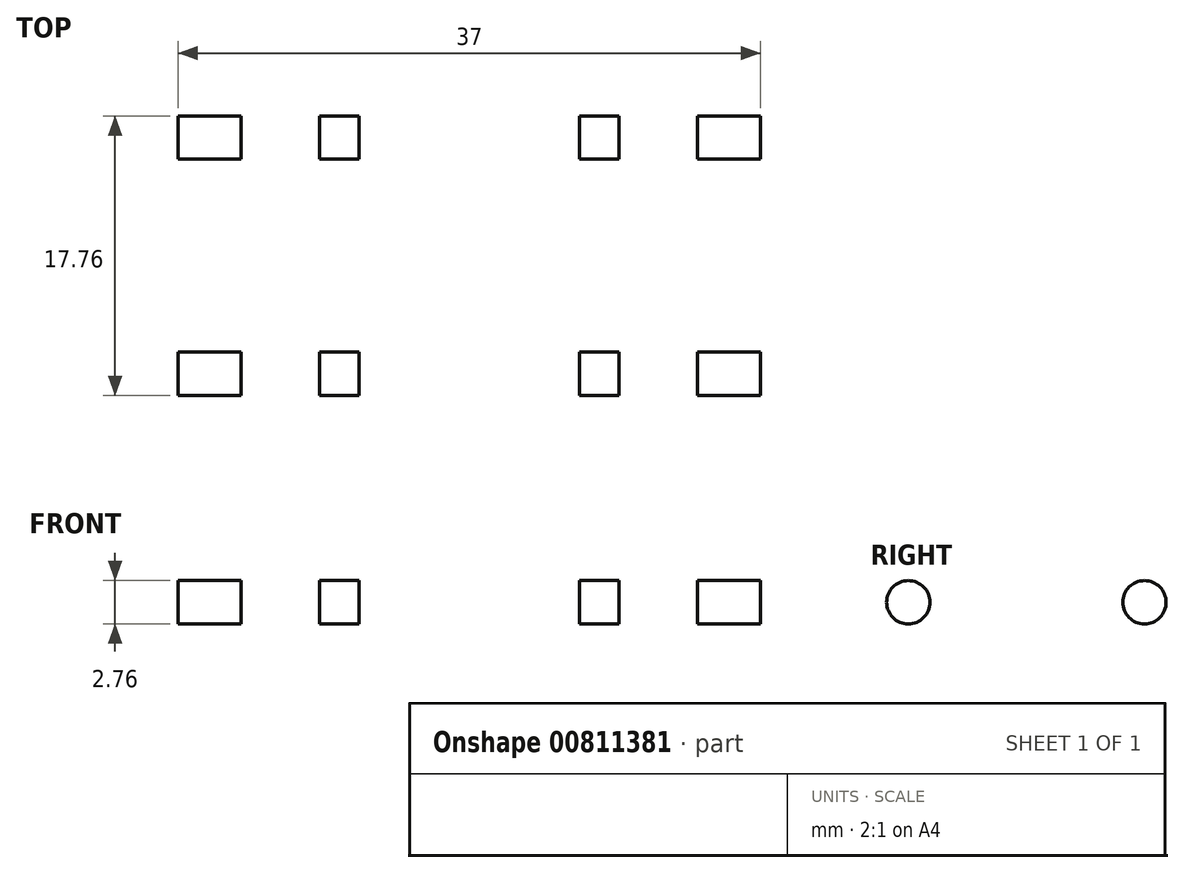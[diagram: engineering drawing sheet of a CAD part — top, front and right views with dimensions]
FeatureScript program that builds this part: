
annotation { "Feature Type Name" : "Feature", "Feature Type Description" : "" }
export const myFeature = defineFeature(function(context is Context, id is Id, definition is map)
    precondition{}
    {
        {
            var Q0;
            Q0=qCreatedBy(makeId("Front.planeOp"),FACE);
            var sketch = newSketch(context, id + "F0", { "sketchPlane" : qUnion([Q0])});
            skLineSegment(sketch, "E0.bottom", {"start": v(18.5, -7.5) * mm, "end": v(-18.5, -7.5) * mm});
            skLineSegment(sketch, "E0.top", {"start": v(18.5, 7.5) * mm, "end": v(-18.5, 7.5) * mm});
            skLineSegment(sketch, "E0.left", {"start": v(18.5, -7.5) * mm, "end": v(18.5, 7.5) * mm});
            skLineSegment(sketch, "E0.right", {"start": v(-18.5, -7.5) * mm, "end": v(-18.5, 7.5) * mm});
            skPoint(sketch, "E0.middle", {"position": v(0, 0) * mm});
            skLineSegment(sketch, "E1.bottom", {"start": v(-10, 7.5) * mm, "end": v(10, 7.5) * mm});
            skLineSegment(sketch, "E1.top", {"start": v(-10, 17.5) * mm, "end": v(10, 17.5) * mm});
            skLineSegment(sketch, "E1.left", {"start": v(-10, 7.5) * mm, "end": v(-10, 17.5) * mm});
            skLineSegment(sketch, "E1.right", {"start": v(10, 7.5) * mm, "end": v(10, 17.5) * mm});
            skLineSegment(sketch, "E2.bottom", {"start": v(-3.5, 17.5) * mm, "end": v(3.5, 17.5) * mm});
            skLineSegment(sketch, "E2.top", {"start": v(-3.5, 7.5) * mm, "end": v(3.5, 7.5) * mm});
            skLineSegment(sketch, "E2.left", {"start": v(-3.5, 17.5) * mm, "end": v(-3.5, 7.5) * mm});
            skLineSegment(sketch, "E2.right", {"start": v(3.5, 17.5) * mm, "end": v(3.5, 7.5) * mm});
            skLineSegment(sketch, "E3.bottom", {"start": v(-14.5, 2.5) * mm, "end": v(-9.5, 2.5) * mm});
            skLineSegment(sketch, "E3.top", {"start": v(-14.5, -2.5) * mm, "end": v(-9.5, -2.5) * mm});
            skLineSegment(sketch, "E3.left", {"start": v(-14.5, 2.5) * mm, "end": v(-14.5, -2.5) * mm});
            skLineSegment(sketch, "E3.right", {"start": v(-9.5, 2.5) * mm, "end": v(-9.5, -2.5) * mm});
            skLineSegment(sketch, "E4.bottom", {"start": v(9.5, 2.5) * mm, "end": v(14.5, 2.5) * mm});
            skLineSegment(sketch, "E4.top", {"start": v(9.5, -2.5) * mm, "end": v(14.5, -2.5) * mm});
            skLineSegment(sketch, "E4.left", {"start": v(9.5, 2.5) * mm, "end": v(9.5, -2.5) * mm});
            skLineSegment(sketch, "E4.right", {"start": v(14.5, 2.5) * mm, "end": v(14.5, -2.5) * mm});
            skLineSegment(sketch, "E5.bottom", {"start": v(7, -2.5) * mm, "end": v(-7, -2.5) * mm});
            skLineSegment(sketch, "E5.top", {"start": v(7, 2.5) * mm, "end": v(-7, 2.5) * mm});
            skLineSegment(sketch, "E5.left", {"start": v(7, -2.5) * mm, "end": v(7, 2.5) * mm});
            skLineSegment(sketch, "E5.right", {"start": v(-7, -2.5) * mm, "end": v(-7, 2.5) * mm});
            skSolve(sketch);
        }
        {
            var Q0;
            Q0=makeQuery(id+"F0.imprint","IMPRINT",FACE,{"disambiguationData":[TD([[makeQuery(id+"F0.imprint","IMPRINT",EDGE,{"derivedFrom":sQuery(id+"F0.wireOp",EDGE,"E0.bottom")}),-1.0]])]});
            var Q1;
            Q1=makeQuery(id+"F0.imprint","IMPRINT",FACE,{"disambiguationData":[TD([[makeQuery(id+"F0.imprint","IMPRINT",EDGE,{"derivedFrom":sQuery(id+"F0.wireOp",EDGE,"E1.bottom")}),1.0]])]});
            extrude(context, id + "F1", {"entities" : qUnion([Q0, Q1]), "depth" : 25 * mm, "offsetDistance" : 25 * mm});
        }
        {
            var Q0;
            Q0=makeQuery(id+"F1.opExtrude","SWEPT_FACE",FACE,{"disambiguationData":[OSD([sQuery(id+"F0.wireOp",EDGE,"E0.right")])]});
            var sketch = newSketch(context, id + "F2", { "sketchPlane" : qUnion([Q0])});
            skLineSegment(sketch, "E6", {"start": v(25, 0) * mm, "end": v(0, 0) * mm});
            skCircle(sketch, "E7", {"center": v(5, 0) * mm, "radius": 1.38 * mm});
            skCircle(sketch, "E8", {"center": v(20, 0) * mm, "radius": 1.38 * mm});
            skCircle(sketch, "E9", {"center": v(5, 14.5) * mm, "radius": 1.5 * mm});
            skCircle(sketch, "E10.1.0.0", {"center": v(10, 14.5) * mm, "radius": 1.5 * mm});
            skCircle(sketch, "E10.2.0.0", {"center": v(15, 14.5) * mm, "radius": 1.5 * mm});
            skCircle(sketch, "E10.3.0.0", {"center": v(20, 14.5) * mm, "radius": 1.5 * mm});
            skLineSegment(sketch, "E10.direction1", {"start": v(5, 14.5) * mm, "end": v(10, 14.5) * mm, "construction": true});
            skSolve(sketch);
        }
        {
            var Q0;
            Q0=makeQuery(id+"F2.imprint","IMPRINT",FACE,{"disambiguationData":[TD([[makeQuery(id+"F2.imprint","IMPRINT",EDGE,{"derivedFrom":sQuery(id+"F2.wireOp",EDGE,"E9")}),1.0]])]});
            var Q1;
            Q1=makeQuery(id+"F2.imprint","IMPRINT",FACE,{"disambiguationData":[TD([[makeQuery(id+"F2.imprint","IMPRINT",EDGE,{"derivedFrom":sQuery(id+"F2.wireOp",EDGE,"E10.1.0.0")}),1.0]])]});
            var Q2;
            Q2=makeQuery(id+"F2.imprint","IMPRINT",FACE,{"disambiguationData":[TD([[makeQuery(id+"F2.imprint","IMPRINT",EDGE,{"derivedFrom":sQuery(id+"F2.wireOp",EDGE,"E10.2.0.0")}),1.0]])]});
            var Q3;
            Q3=makeQuery(id+"F2.imprint","IMPRINT",FACE,{"disambiguationData":[TD([[makeQuery(id+"F2.imprint","IMPRINT",EDGE,{"derivedFrom":sQuery(id+"F2.wireOp",EDGE,"E10.3.0.0")}),1.0]])]});
            var Q4;
            {var subQ0=sQuery(id+"F2.wireOp",EDGE,"E8");var subQ1=sQuery(id+"F2.wireOp",EDGE,"E6");var subQ2=makeQuery(id+"F2.imprint","INTERSECT",VERTEX,{"disambiguationData":[OD(0.0)],"derivedFrom":[subQ1,subQ0]});Q4=makeQuery(id+"F2.imprint","IMPRINT",FACE,{"disambiguationData":[TD([[makeQuery(id+"F2.imprint","IMPRINT",EDGE,{"disambiguationData":[TD([[subQ2,-1.0]])],"derivedFrom":subQ1}),-1.0]])]});}
            var Q5;
            {var subQ0=sQuery(id+"F2.wireOp",EDGE,"E7");var subQ1=sQuery(id+"F2.wireOp",EDGE,"E6");var subQ2=makeQuery(id+"F2.imprint","INTERSECT",VERTEX,{"disambiguationData":[OD(0.0)],"derivedFrom":[subQ1,subQ0]});Q5=makeQuery(id+"F2.imprint","IMPRINT",FACE,{"disambiguationData":[TD([[makeQuery(id+"F2.imprint","IMPRINT",EDGE,{"disambiguationData":[TD([[subQ2,-1.0]])],"derivedFrom":subQ1}),-1.0]])]});}
            var Q6;
            {var subQ0=sQuery(id+"F2.wireOp",EDGE,"E7");var subQ1=sQuery(id+"F2.wireOp",EDGE,"E6");var subQ2=makeQuery(id+"F2.imprint","INTERSECT",VERTEX,{"disambiguationData":[OD(0.0)],"derivedFrom":[subQ1,subQ0]});Q6=makeQuery(id+"F2.imprint","IMPRINT",FACE,{"disambiguationData":[TD([[makeQuery(id+"F2.imprint","IMPRINT",EDGE,{"disambiguationData":[TD([[subQ2,-1.0]])],"derivedFrom":subQ1}),1.0]])]});}
            var Q7;
            {var subQ0=sQuery(id+"F2.wireOp",EDGE,"E8");var subQ1=sQuery(id+"F2.wireOp",EDGE,"E6");var subQ2=makeQuery(id+"F2.imprint","INTERSECT",VERTEX,{"disambiguationData":[OD(0.0)],"derivedFrom":[subQ1,subQ0]});Q7=makeQuery(id+"F2.imprint","IMPRINT",FACE,{"disambiguationData":[TD([[makeQuery(id+"F2.imprint","IMPRINT",EDGE,{"disambiguationData":[TD([[subQ2,-1.0]])],"derivedFrom":subQ1}),1.0]])]});}
            var Q8;
            Q8=makeQuery(id+"F1.opExtrude","SWEPT_FACE",FACE,{"disambiguationData":[OSD([sQuery(id+"F0.wireOp",EDGE,"E0.left")])]});
            extrude(context, id + "F3", {"entities" : qUnion([Q0, Q1, Q2, Q3, Q4, Q5, Q6, Q7]), "operationType" : NewBodyOperationType.REMOVE, "endBound" : BoundingType.UP_TO_SURFACE, "oppositeDirection" : true, "depth" : 25 * mm, "endBoundEntityFace" : qUnion([Q8]), "offsetDistance" : 25 * mm});
        }
    });
